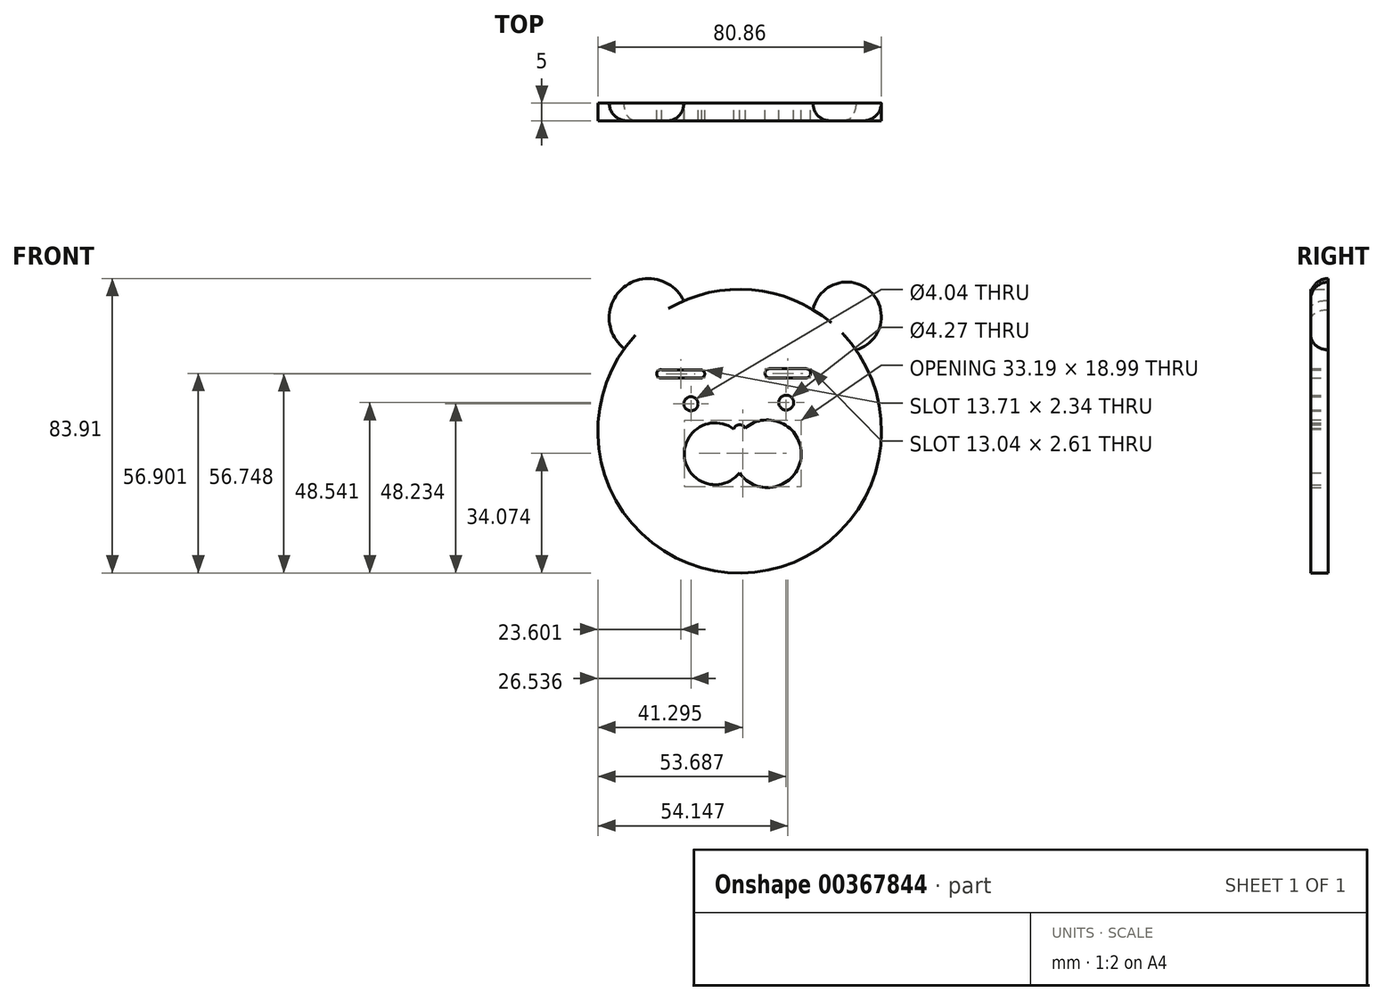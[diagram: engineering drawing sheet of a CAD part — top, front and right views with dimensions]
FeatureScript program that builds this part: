
annotation { "Feature Type Name" : "Feature", "Feature Type Description" : "" }
export const myFeature = defineFeature(function(context is Context, id is Id, definition is map)
    precondition{}
    {
        {
            var Q0;
            Q0=qCreatedBy(makeId("Front.planeOp"),FACE);
            var sketch = newSketch(context, id + "F0", { "sketchPlane" : qUnion([Q0])});
            skArc(sketch, "E0", {"start": v(-32.92, 23.48) * mm, "mid": v(-0.2, -40.43) * mm, "end": v(33.14, 23.17) * mm});
            skCircle(sketch, "E1", {"center": v(446.68, -190.68) * mm, "radius": 18.77 * mm});
            skArc(sketch, "E2", {"start": v(-15.93, 37.17) * mm, "mid": v(-33.03, 41) * mm, "end": v(-32.92, 23.48) * mm});
            skArc(sketch, "E3", {"start": v(33.14, 23.17) * mm, "mid": v(37.25, 39.83) * mm, "end": v(20.9, 34.62) * mm});
            skCircle(sketch, "E4", {"center": v(-13.9, 7.8) * mm, "radius": 2.02 * mm});
            skArc(sketch, "E5", {"start": v(-0.07, -1) * mm, "mid": v(-15.8, -6.46) * mm, "end": v(-0.07, -11.92) * mm});
            skArc(sketch, "E6", {"start": v(-0.07, -11.92) * mm, "mid": v(17.54, -6.46) * mm, "end": v(-0.07, -1) * mm});
            skCircle(sketch, "E7", {"center": v(13.26, 8.11) * mm, "radius": 2.14 * mm});
            skCircle(sketch, "E8", {"center": v(0, 0) * mm, "radius": 1.8 * mm});
            skLineSegment(sketch, "E9", {"start": v(-22.18, 17.47) * mm, "end": v(-11.13, 17.47) * mm});
            skLineSegment(sketch, "E10", {"start": v(8.5, 17.78) * mm, "end": v(18.93, 17.78) * mm});
            skArc(sketch, "E11", {"start": v(18.93, 15.17) * mm, "mid": v(20.24, 16.47) * mm, "end": v(18.93, 17.78) * mm});
            skLineSegment(sketch, "E12", {"start": v(18.93, 15.17) * mm, "end": v(8.5, 15.17) * mm});
            skArc(sketch, "E13", {"start": v(8.5, 17.78) * mm, "mid": v(7.2, 16.47) * mm, "end": v(8.5, 15.17) * mm});
            skArc(sketch, "E14", {"start": v(-22.18, 17.47) * mm, "mid": v(-23.69, 16.32) * mm, "end": v(-22.18, 15.17) * mm});
            skLineSegment(sketch, "E15", {"start": v(-22.18, 15.17) * mm, "end": v(-10.83, 15.17) * mm});
            skArc(sketch, "E16", {"start": v(-10.83, 15.17) * mm, "mid": v(-9.97, 16.45) * mm, "end": v(-11.13, 17.47) * mm});
            skArc(sketch, "E17.trimOffspring", {"start": v(20.9, 34.62) * mm, "mid": v(2.8, 40.34) * mm, "end": v(-15.93, 37.17) * mm});
            skSolve(sketch);
        }
        {
            var Q0;
            Q0=makeQuery(id+"F0.imprint","IMPRINT",FACE,{"disambiguationData":[TD([[makeQuery(id+"F0.imprint","IMPRINT",EDGE,{"derivedFrom":sQuery(id+"F0.wireOp",EDGE,"E0")}),1.0]])]});
            extrude(context, id + "F1", {"entities" : qUnion([Q0]), "depth" : 5 * mm});
        }
        {
            var Q0;
            Q0=makeQuery(id+"F1.opExtrude","CAP_EDGE",EDGE,{"disambiguationData":[OSD([sQuery(id+"F0.wireOp",EDGE,"E3")])],"isStart":false});
            fillet(context, id + "F2", {"entities" : qUnion([Q0]), "radius" : 5 * mm, "tangentPropagation" : true, "allowEdgeOverflow" : false});
        }
        {
            var Q0;
            Q0=makeQuery(id+"F1.opExtrude","CAP_EDGE",EDGE,{"disambiguationData":[OSD([sQuery(id+"F0.wireOp",EDGE,"E2")])],"isStart":false});
            fillet(context, id + "F3", {"entities" : qUnion([Q0]), "radius" : 5 * mm, "tangentPropagation" : true, "allowEdgeOverflow" : false});
        }
    });
